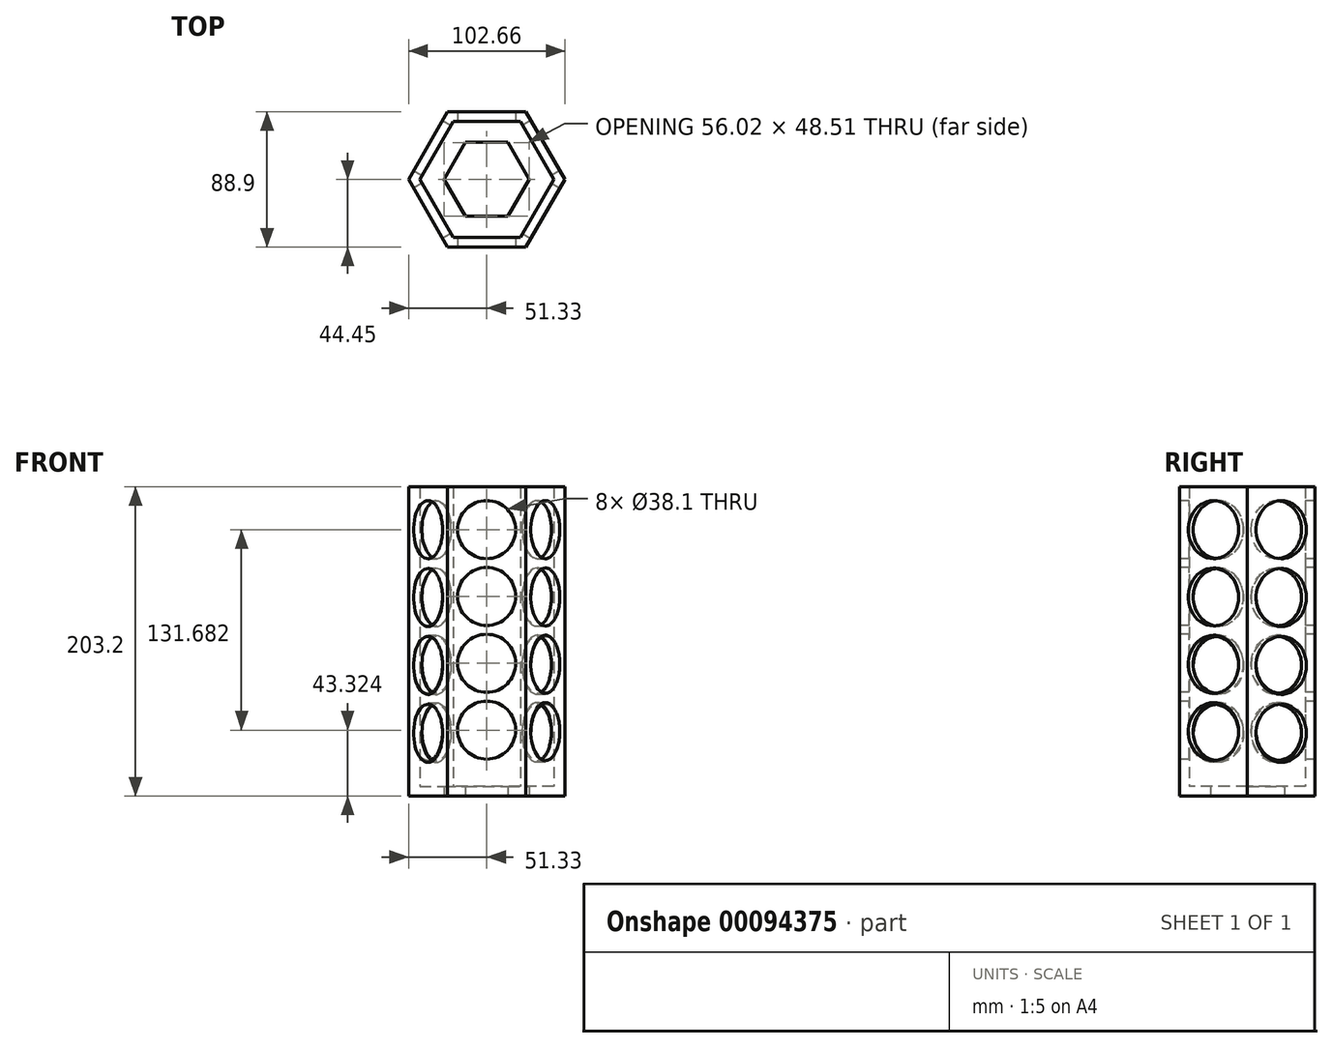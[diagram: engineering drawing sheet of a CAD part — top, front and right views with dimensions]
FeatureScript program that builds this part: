
annotation { "Feature Type Name" : "Feature", "Feature Type Description" : "" }
export const myFeature = defineFeature(function(context is Context, id is Id, definition is map)
    precondition{}
    {
        {
            var Q0;
            Q0=qCreatedBy(makeId("Top.planeOp"),FACE);
            var sketch = newSketch(context, id + "F0", { "sketchPlane" : qUnion([Q0])});
            skCircle(sketch, "E0.cCircle", {"center": v(0, 0) * mm, "radius": 38.1 * mm, "construction": true});
            skLineSegment(sketch, "E0.0", {"start": v(22, -38.1) * mm, "end": v(-22, -38.1) * mm});
            skLineSegment(sketch, "E0.1", {"start": v(-22, -38.1) * mm, "end": v(-44, 0) * mm});
            skLineSegment(sketch, "E0.2", {"start": v(-44, 0) * mm, "end": v(-22, 38.1) * mm});
            skLineSegment(sketch, "E0.3", {"start": v(-22, 38.1) * mm, "end": v(22, 38.1) * mm});
            skLineSegment(sketch, "E0.4", {"start": v(22, 38.1) * mm, "end": v(44, 0) * mm});
            skLineSegment(sketch, "E0.5", {"start": v(44, 0) * mm, "end": v(22, -38.1) * mm});
            skPoint(sketch, "E0.0.midPoint", {"position": v(0, -38.1) * mm});
            skLineSegment(sketch, "E1.0", {"start": v(-25.66, 44.45) * mm, "end": v(25.66, 44.45) * mm});
            skLineSegment(sketch, "E1.1", {"start": v(51.33, 0) * mm, "end": v(25.66, -44.45) * mm});
            skLineSegment(sketch, "E1.2", {"start": v(25.66, -44.45) * mm, "end": v(-25.66, -44.45) * mm});
            skLineSegment(sketch, "E1.3", {"start": v(25.66, 44.45) * mm, "end": v(51.33, 0) * mm});
            skLineSegment(sketch, "E1.4", {"start": v(-25.66, -44.45) * mm, "end": v(-51.33, 0) * mm});
            skLineSegment(sketch, "E1.5", {"start": v(-51.33, 0) * mm, "end": v(-25.66, 44.45) * mm});
            skSolve(sketch);
        }
        {
            var Q0;
            Q0=makeQuery(id+"F0.imprint","IMPRINT",FACE,{"disambiguationData":[TD([[makeQuery(id+"F0.imprint","IMPRINT",EDGE,{"derivedFrom":sQuery(id+"F0.wireOp",EDGE,"E0.0")}),1.0]])]});
            extrude(context, id + "F1", {"entities" : qUnion([Q0]), "depth" : 203.2 * mm});
        }
        {
            var Q0;
            Q0=makeQuery(id+"F0.imprint","IMPRINT",FACE,{"disambiguationData":[TD([[makeQuery(id+"F0.imprint","IMPRINT",EDGE,{"derivedFrom":sQuery(id+"F0.wireOp",EDGE,"E0.0")}),-1.0]])]});
            extrude(context, id + "F2", {"entities" : qUnion([Q0]), "operationType" : NewBodyOperationType.ADD, "depth" : 6.35 * mm});
        }
        {
            var Q0;
            Q0=makeQuery(id+"F1.opExtrude","SWEPT_FACE",FACE,{"disambiguationData":[OSD([sQuery(id+"F0.wireOp",EDGE,"E1.2")])]});
            var sketch = newSketch(context, id + "F3", { "sketchPlane" : qUnion([Q0])});
            skCircle(sketch, "E2", {"center": v(0, 175) * mm, "radius": 19.05 * mm});
            skCircle(sketch, "E3.0.1.0", {"center": v(0, 131.11) * mm, "radius": 19.05 * mm});
            skCircle(sketch, "E3.0.2.0", {"center": v(0, 87.22) * mm, "radius": 19.05 * mm});
            skCircle(sketch, "E3.0.3.0", {"center": v(0, 43.32) * mm, "radius": 19.05 * mm});
            skLineSegment(sketch, "E3.direction1", {"start": v(0, 175) * mm, "end": v(25.4, 175) * mm, "construction": true});
            skLineSegment(sketch, "E3.direction2", {"start": v(0, 175) * mm, "end": v(0, 131.11) * mm, "construction": true});
            skLineSegment(sketch, "E4", {"start": v(0, 175) * mm, "end": v(25.4, 175) * mm});
            skLineSegment(sketch, "E5", {"start": v(0, 194.06) * mm, "end": v(0, 203.2) * mm});
            skSolve(sketch);
        }
        {
            var Q0;
            Q0=makeQuery(id+"F1.opExtrude","SWEPT_FACE",FACE,{"disambiguationData":[OSD([sQuery(id+"F0.wireOp",EDGE,"E1.1")])]});
            var sketch = newSketch(context, id + "F4", { "sketchPlane" : qUnion([Q0])});
            skCircle(sketch, "E6", {"center": v(0, 175) * mm, "radius": 19.05 * mm});
            skLineSegment(sketch, "E7", {"start": v(0, 203.2) * mm, "end": v(0, 194.06) * mm});
            skCircle(sketch, "E8.0.1.0", {"center": v(0, 130.79) * mm, "radius": 19.05 * mm});
            skCircle(sketch, "E8.0.2.0", {"center": v(0, 86.57) * mm, "radius": 19.05 * mm});
            skCircle(sketch, "E8.0.3.0", {"center": v(0, 42.35) * mm, "radius": 19.05 * mm});
            skLineSegment(sketch, "E8.direction1", {"start": v(0, 175) * mm, "end": v(25.4, 175) * mm, "construction": true});
            skLineSegment(sketch, "E8.direction2", {"start": v(0, 175) * mm, "end": v(0, 130.79) * mm, "construction": true});
            skSolve(sketch);
        }
        {
            var Q0;
            Q0=makeQuery(id+"F1.opExtrude","SWEPT_FACE",FACE,{"disambiguationData":[OSD([sQuery(id+"F0.wireOp",EDGE,"E1.4")])]});
            var sketch = newSketch(context, id + "F5", { "sketchPlane" : qUnion([Q0])});
            skCircle(sketch, "E9", {"center": v(0, 175) * mm, "radius": 19.05 * mm});
            skLineSegment(sketch, "E10", {"start": v(0, 194.06) * mm, "end": v(0, 203.2) * mm});
            skCircle(sketch, "E11.0.1.0", {"center": v(0, 130.41) * mm, "radius": 19.05 * mm});
            skCircle(sketch, "E11.0.2.0", {"center": v(0, 85.82) * mm, "radius": 19.05 * mm});
            skCircle(sketch, "E11.0.3.0", {"center": v(0, 41.23) * mm, "radius": 19.05 * mm});
            skLineSegment(sketch, "E11.direction1", {"start": v(0, 175) * mm, "end": v(25.4, 175) * mm, "construction": true});
            skLineSegment(sketch, "E11.direction2", {"start": v(0, 175) * mm, "end": v(0, 130.41) * mm, "construction": true});
            skSolve(sketch);
        }
        {
            var Q0;
            Q0 = qSketchRegion(id + "F3", true);
            extrude(context, id + "F6", {"entities" : qUnion([Q0]), "operationType" : NewBodyOperationType.REMOVE, "oppositeDirection" : true, "depth" : 101.6 * mm});
        }
        {
            var Q0;
            Q0 = qSketchRegion(id + "F4", true);
            extrude(context, id + "F7", {"entities" : qUnion([Q0]), "operationType" : NewBodyOperationType.REMOVE, "oppositeDirection" : true, "depth" : 101.6 * mm});
        }
        {
            var Q0;
            Q0 = qSketchRegion(id + "F5", true);
            extrude(context, id + "F8", {"entities" : qUnion([Q0]), "operationType" : NewBodyOperationType.REMOVE, "oppositeDirection" : true, "depth" : 101.6 * mm});
        }
        {
            var Q0;
            {var subQ0=sQuery(id+"F0.wireOp",EDGE,"E0.5");var subQ1=sQuery(id+"F0.wireOp",EDGE,"E0.4");var subQ2=sQuery(id+"F0.wireOp",EDGE,"E0.3");var subQ3=sQuery(id+"F0.wireOp",EDGE,"E0.2");var subQ4=sQuery(id+"F0.wireOp",EDGE,"E0.1");var subQ5=sQuery(id+"F0.wireOp",EDGE,"E0.0");Q0=makeQuery(id+"F2.boolean.opBoolean","MERGE",FACE,{"derivedFrom":[makeQuery(id+"F1.opExtrude","CAP_FACE",FACE,{"disambiguationData":[OSD([subQ5,subQ4,subQ3,subQ2,subQ1,subQ0,sQuery(id+"F0.wireOp",EDGE,"E1.0"),sQuery(id+"F0.wireOp",EDGE,"E1.1"),sQuery(id+"F0.wireOp",EDGE,"E1.2"),sQuery(id+"F0.wireOp",EDGE,"E1.3"),sQuery(id+"F0.wireOp",EDGE,"E1.4"),sQuery(id+"F0.wireOp",EDGE,"E1.5")])],"isStart":true}),makeQuery(id+"F2.opExtrude","CAP_FACE",FACE,{"disambiguationData":[OSD([subQ5,subQ4,subQ3,subQ2,subQ1,subQ0])],"isStart":true})]});}
            var sketch = newSketch(context, id + "F9", { "sketchPlane" : qUnion([Q0])});
            skCircle(sketch, "E12.cCircle", {"center": v(0, 0) * mm, "radius": 24.26 * mm, "construction": true});
            skPoint(sketch, "E12.cCircle.perimeterSnap0", {"position": v(0, -44.45) * mm});
            skLineSegment(sketch, "E12.0", {"start": v(14, -24.26) * mm, "end": v(-14, -24.26) * mm});
            skLineSegment(sketch, "E12.1", {"start": v(-14, -24.26) * mm, "end": v(-28, 0) * mm});
            skLineSegment(sketch, "E12.2", {"start": v(-28, 0) * mm, "end": v(-14, 24.26) * mm});
            skLineSegment(sketch, "E12.3", {"start": v(-14, 24.26) * mm, "end": v(14, 24.26) * mm});
            skLineSegment(sketch, "E12.4", {"start": v(14, 24.26) * mm, "end": v(28, 0) * mm});
            skLineSegment(sketch, "E12.5", {"start": v(28, 0) * mm, "end": v(14, -24.26) * mm});
            skPoint(sketch, "E12.0.midPoint", {"position": v(0, -24.26) * mm});
            skPoint(sketch, "E12.0.midPoint.positionSnap0", {"position": v(0, -44.45) * mm});
            skSolve(sketch);
        }
        {
            var Q0;
            Q0=makeQuery(id+"F9.imprint","IMPRINT",FACE,{"disambiguationData":[TD([[makeQuery(id+"F9.imprint","IMPRINT",EDGE,{"derivedFrom":sQuery(id+"F9.wireOp",EDGE,"E12.0")}),-1.0]])]});
            extrude(context, id + "F10", {"entities" : qUnion([Q0]), "operationType" : NewBodyOperationType.REMOVE, "oppositeDirection" : true, "depth" : 25.4 * mm});
        }
    });
